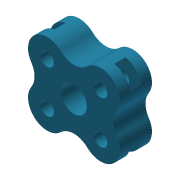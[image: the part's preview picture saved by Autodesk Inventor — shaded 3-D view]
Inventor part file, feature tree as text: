
AUTODESK INVENTOR PART (.ipt)
format: ipt  version: 2014 (Build 180170000, 170)  size: 173,056 bytes
history: native  units: mm
features: extrude x2, sketch x2
ambient origin geometry x8: Origin, YZ Plane, XZ Plane, XY Plane, X Axis, Y Axis, Z Axis, Center Point
bodies: Solid1 (feature_tree)
feature tree (4):
  extrude  "Extrusion1"  Depth=13.0mm
  extrude  "Extrusion2"  Depth=5.25mm
  sketch  "Sketch1"  dims[d0=6.2mm d1=13.0mm]
  sketch  "Sketch2"  dims[d2=20.0mm d4=12.0mm d5=25.0mm d7=15.0mm d8=0.0mm d9=9.0mm d10=9.0mm d11=9.0mm d12=10.5mm d13=45.0deg d14=45.0deg d15=10.0mm d16=5.25mm d17=0.0mm]
